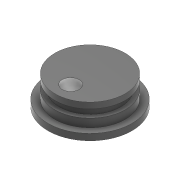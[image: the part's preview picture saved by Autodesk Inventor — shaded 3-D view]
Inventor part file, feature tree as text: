
AUTODESK INVENTOR PART (.ipt)
format: ipt  version: 2022.3 (Build 263350000, 350)  size: 141,312 bytes
history: native  units: mm
features: extrude x5, sketch x5, other x1, plane x1
ambient origin geometry x8: Origin, YZ Plane, XZ Plane, XY Plane, X Axis, Y Axis, Z Axis, Center Point
bodies: Body1 (feature_tree)
feature tree (12):
  other  "Sólido1"
  extrude  "Extrusión1"  Depth=4.0mm TaperAngle=0.0deg
  extrude  "Extrusión2"  Depth=13.8mm TaperAngle=0.0deg
  plane  "Plano de trabajo1"
  extrude  "Extrusión6"  Depth=37.85mm
  extrude  "Extrusión7"  Depth=5.0mm
  extrude  "Extrusión8"  Depth=4.45mm
  sketch  "Boceto1"  dims[d0=52.0mm d1=4.0mm d2=0.0mm]
  sketch  "Boceto2"  dims[d3=43.55mm d4=13.8mm d5=0.0mm]
  sketch  "Boceto6"  dims[d17=-3.6mm d18=37.85mm]
  sketch  "Boceto7"  dims[d19=5.0mm d20=0.0mm d21=5.5mm]
  sketch  "Boceto8"  dims[d22=17.05mm d23=19.15mm d24=4.45mm d25=0.0mm d26=10.55mm d27=15.0mm d28=0.0mm]
